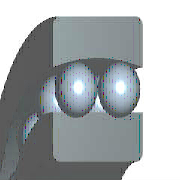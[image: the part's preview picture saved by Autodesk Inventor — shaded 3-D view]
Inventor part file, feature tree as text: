
AUTODESK INVENTOR PART (.ipt)
format: ipt  version: 2021 (Build 250183000, 183)  size: 408,576 bytes
history: native  units: mm (DEFAULTED — no unit token found)
features: plane x5, other x3, sketch x3
ambient origin geometry x7: Origin, XZ Plane, XY Plane, X Axis, Y Axis, Z Axis, Center Point
bodies: Solid1 (feature_tree)
feature tree (11):
  plane  "WorkPlane2"
  other  "WorkPoint1"
  plane  "Work Plane2"
  plane  "WorkPlane4"
  other  "WorkPoint2"
  other  "WorkAxis1"
  plane  "WorkPlane3"
  plane  "WorkPlane1"
  sketch  "草圖2"
  sketch  "草圖6"
  sketch  "草圖7"
